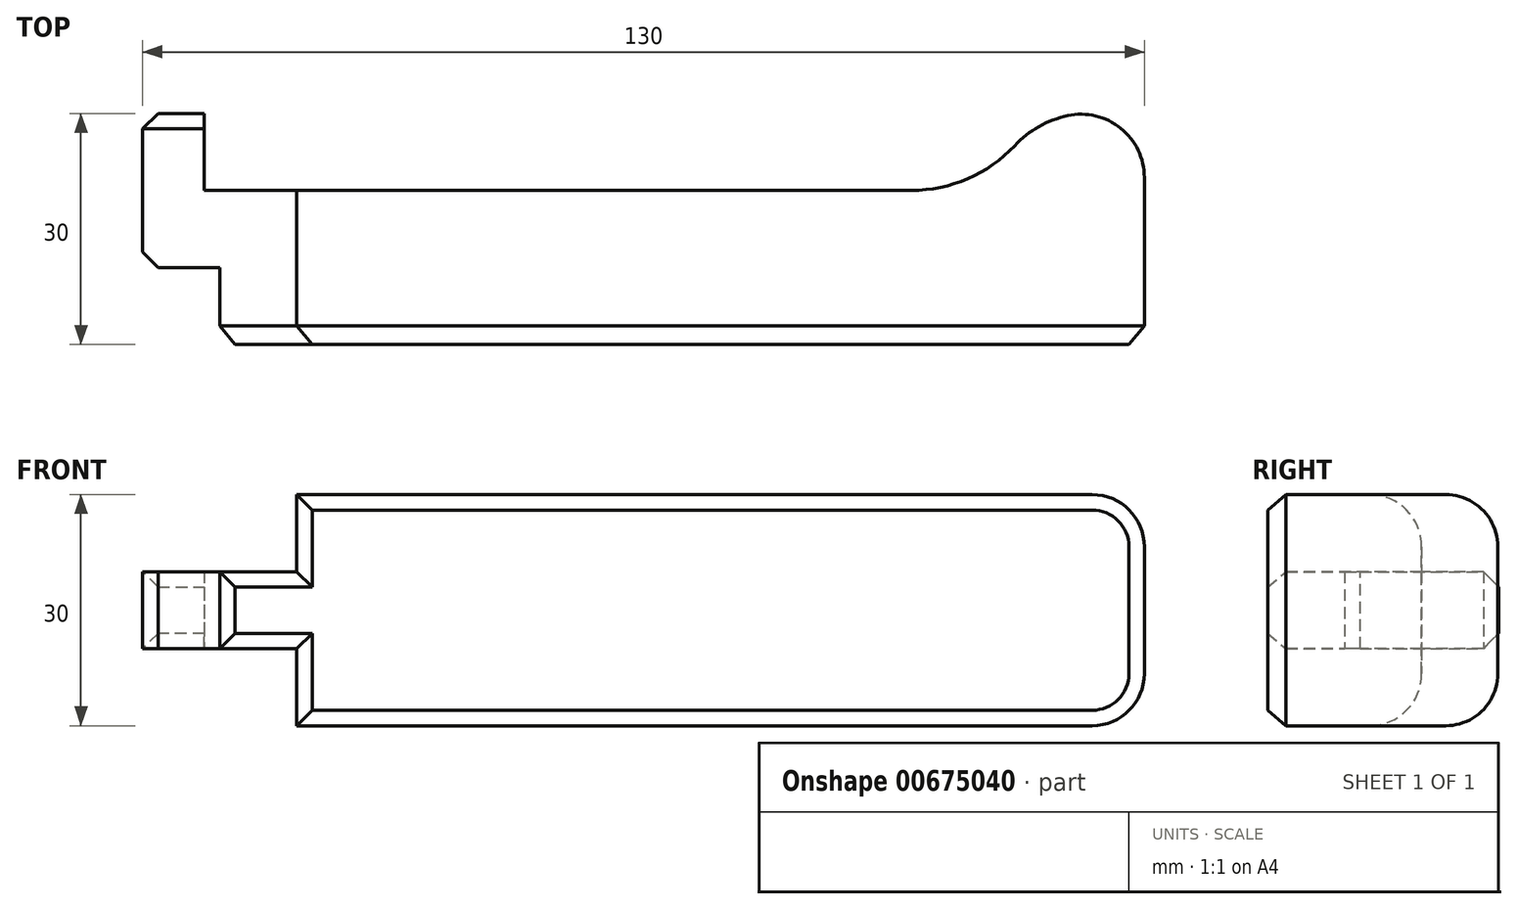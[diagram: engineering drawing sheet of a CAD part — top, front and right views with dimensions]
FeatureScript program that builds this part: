
annotation { "Feature Type Name" : "Feature", "Feature Type Description" : "" }
export const myFeature = defineFeature(function(context is Context, id is Id, definition is map)
    precondition{}
    {
        {
            var Q0;
            Q0=qCreatedBy(makeId("Top.planeOp"),FACE);
            var sketch = newSketch(context, id + "F0", { "sketchPlane" : qUnion([Q0])});
            skLineSegment(sketch, "E0", {"start": v(-58.1, 0) * mm, "end": v(61.9, 0) * mm});
            skLineSegment(sketch, "E1", {"start": v(-58.1, 0) * mm, "end": v(-58.1, 10) * mm});
            skLineSegment(sketch, "E2", {"start": v(-58.1, 10) * mm, "end": v(-68.1, 10) * mm});
            skLineSegment(sketch, "E3", {"start": v(-68.1, 10) * mm, "end": v(-68.1, 30) * mm});
            skLineSegment(sketch, "E4", {"start": v(-68.1, 30) * mm, "end": v(-60.1, 30) * mm});
            skLineSegment(sketch, "E5", {"start": v(-60.1, 30) * mm, "end": v(-60.1, 20) * mm});
            skLineSegment(sketch, "E6", {"start": v(-60.1, 20) * mm, "end": v(-48.1, 20) * mm});
            skLineSegment(sketch, "E7", {"start": v(-48.1, 20) * mm, "end": v(-48.1, 0) * mm});
            skLineSegment(sketch, "E8", {"start": v(61.9, 0) * mm, "end": v(61.9, 20) * mm});
            skLineSegment(sketch, "E9", {"start": v(61.9, 20) * mm, "end": v(-48.1, 20) * mm});
            skLineSegment(sketch, "E10", {"start": v(-48.1, 20) * mm, "end": v(-48.1, 20) * mm});
            skLineSegment(sketch, "E11", {"start": v(61.9, 20) * mm, "end": v(61.9, 30) * mm});
            skLineSegment(sketch, "E12", {"start": v(61.9, 30) * mm, "end": v(41.9, 30) * mm});
            skLineSegment(sketch, "E13", {"start": v(41.9, 20) * mm, "end": v(41.9, 30) * mm});
            skSolve(sketch);
        }
        {
            var Q0;
            {var subQ0=sQuery(id+"F0.wireOp",EDGE,"E1");Q0=makeQuery(id+"F0.imprint","IMPRINT",FACE,{"disambiguationData":[TD([[makeQuery(id+"F0.imprint","IMPRINT",EDGE,{"derivedFrom":subQ0}),-1.0]])]});}
            extrude(context, id + "F1", {"entities" : qUnion([Q0]), "endBound" : BoundingType.SYMMETRIC, "depth" : 10 * mm, "offsetDistance" : 25 * mm});
        }
        {
            var Q0;
            {var subQ2=sQuery(id+"F0.wireOp",EDGE,"E7");Q0=makeQuery(id+"F0.imprint","IMPRINT",FACE,{"disambiguationData":[TD([[makeQuery(id+"F0.imprint","IMPRINT",EDGE,{"derivedFrom":subQ2}),1.0]])]});}
            var Q1;
            {var subQ0=sQuery(id+"F0.wireOp",EDGE,"E11");Q1=makeQuery(id+"F0.imprint","IMPRINT",FACE,{"disambiguationData":[TD([[makeQuery(id+"F0.imprint","IMPRINT",EDGE,{"derivedFrom":subQ0}),1.0]])]});}
            extrude(context, id + "F2", {"entities" : qUnion([Q0, Q1]), "operationType" : NewBodyOperationType.ADD, "endBound" : BoundingType.SYMMETRIC, "depth" : 30 * mm, "offsetDistance" : 25 * mm});
        }
        {
            var Q0;
            Q0=makeQuery(id+"F2.opExtrude","SWEPT_EDGE",EDGE,{"disambiguationData":[OSD([sQuery(id+"F0.wireOp",EDGE,"E12"),sQuery(id+"F0.wireOp",EDGE,"E13")])]});
            fillet(context, id + "F3", {"entities" : qUnion([Q0]), "radius" : 13.28 * mm, "tangentPropagation" : true, "allowEdgeOverflow" : false});
        }
        {
            var Q0;
            Q0=makeQuery(id+"F2.opExtrude","SWEPT_EDGE",EDGE,{"disambiguationData":[OSD([sQuery(id+"F0.wireOp",EDGE,"E11"),sQuery(id+"F0.wireOp",EDGE,"E12")])]});
            fillet(context, id + "F4", {"entities" : qUnion([Q0]), "radius" : 8.2 * mm, "tangentPropagation" : true, "allowEdgeOverflow" : false});
        }
        {
            var Q0;
            Q0=makeQuery(id+"F3.opFillet","BLEND_EDGE",EDGE,{"blendedFrom":[makeQuery(id+"F2.opExtrude","SWEPT_EDGE",EDGE,{"disambiguationData":[OSD([sQuery(id+"F0.wireOp",EDGE,"E12"),sQuery(id+"F0.wireOp",EDGE,"E13")])]}),makeQuery(id+"F2.boolean.opBoolean","MERGE",FACE,{"derivedFrom":[makeQuery(id+"F1.opExtrude","SWEPT_FACE",FACE,{"disambiguationData":[OSD([sQuery(id+"F0.wireOp",EDGE,"E6")])]}),makeQuery(id+"F2.opExtrude","SWEPT_FACE",FACE,{"disambiguationData":[OSD([sQuery(id+"F0.wireOp",EDGE,"E9")])]})]})],"blendedInto":[makeQuery(id+"F2.boolean.opBoolean","MERGE",FACE,{"derivedFrom":[makeQuery(id+"F1.opExtrude","SWEPT_FACE",FACE,{"disambiguationData":[OSD([sQuery(id+"F0.wireOp",EDGE,"E6")])]}),makeQuery(id+"F2.opExtrude","SWEPT_FACE",FACE,{"disambiguationData":[OSD([sQuery(id+"F0.wireOp",EDGE,"E9")])]})]})]});
            fillet(context, id + "F5", {"entities" : qUnion([Q0]), "radius" : 18.4 * mm, "tangentPropagation" : true, "allowEdgeOverflow" : false});
        }
        {
            var Q0;
            Q0=makeQuery(id+"F2.opExtrude","CAP_EDGE",EDGE,{"disambiguationData":[OSD([sQuery(id+"F0.wireOp",EDGE,"E9")])],"isStart":true});
            var Q1;
            Q1=makeQuery(id+"F2.opExtrude","CAP_EDGE",EDGE,{"disambiguationData":[OSD([sQuery(id+"F0.wireOp",EDGE,"E9")])],"isStart":false});
            fillet(context, id + "F6", {"entities" : qUnion([Q0, Q1]), "radius" : 6.76 * mm, "tangentPropagation" : true, "allowEdgeOverflow" : false});
        }
        {
            var Q0;
            Q0=makeQuery(id+"F2.opExtrude","CAP_EDGE",EDGE,{"disambiguationData":[OSD([sQuery(id+"F0.wireOp",EDGE,"E0")])],"isStart":true});
            var Q1;
            Q1=makeQuery(id+"F2.opExtrude","CAP_EDGE",EDGE,{"disambiguationData":[OSD([sQuery(id+"F0.wireOp",EDGE,"E0")])],"isStart":false});
            var Q2;
            {var subQ0=sQuery(id+"F0.wireOp",EDGE,"E0");Q2=makeQuery(id+"F6.opFillet","BLEND_EDGE",EDGE,{"blendedFrom":[makeQuery(id+"F2.opExtrude","CAP_EDGE",EDGE,{"disambiguationData":[OSD([sQuery(id+"F0.wireOp",EDGE,"E8"),sQuery(id+"F0.wireOp",EDGE,"E11")])],"isStart":false}),makeQuery(id+"F2.boolean.opBoolean","MERGE",FACE,{"derivedFrom":[makeQuery(id+"F1.opExtrude","SWEPT_FACE",FACE,{"disambiguationData":[OSD([subQ0])]}),makeQuery(id+"F2.opExtrude","SWEPT_FACE",FACE,{"disambiguationData":[OSD([subQ0])]})]})],"blendedInto":[makeQuery(id+"F2.boolean.opBoolean","MERGE",FACE,{"derivedFrom":[makeQuery(id+"F1.opExtrude","SWEPT_FACE",FACE,{"disambiguationData":[OSD([subQ0])]}),makeQuery(id+"F2.opExtrude","SWEPT_FACE",FACE,{"disambiguationData":[OSD([subQ0])]})]})]});}
            var Q3;
            Q3=makeQuery(id+"F2.opExtrude","SWEPT_EDGE",EDGE,{"disambiguationData":[OSD([sQuery(id+"F0.wireOp",EDGE,"E0"),sQuery(id+"F0.wireOp",EDGE,"E8")])]});
            var Q4;
            {var subQ0=sQuery(id+"F0.wireOp",EDGE,"E0");Q4=makeQuery(id+"F6.opFillet","BLEND_EDGE",EDGE,{"blendedFrom":[makeQuery(id+"F2.opExtrude","CAP_EDGE",EDGE,{"disambiguationData":[OSD([sQuery(id+"F0.wireOp",EDGE,"E8"),sQuery(id+"F0.wireOp",EDGE,"E11")])],"isStart":true}),makeQuery(id+"F2.boolean.opBoolean","MERGE",FACE,{"derivedFrom":[makeQuery(id+"F1.opExtrude","SWEPT_FACE",FACE,{"disambiguationData":[OSD([subQ0])]}),makeQuery(id+"F2.opExtrude","SWEPT_FACE",FACE,{"disambiguationData":[OSD([subQ0])]})]})],"blendedInto":[makeQuery(id+"F2.boolean.opBoolean","MERGE",FACE,{"derivedFrom":[makeQuery(id+"F1.opExtrude","SWEPT_FACE",FACE,{"disambiguationData":[OSD([subQ0])]}),makeQuery(id+"F2.opExtrude","SWEPT_FACE",FACE,{"disambiguationData":[OSD([subQ0])]})]})]});}
            var Q5;
            {var subQ0=sQuery(id+"F0.wireOp",EDGE,"E7");var subQ1=sQuery(id+"F0.wireOp",EDGE,"E0");Q5=makeQuery(id+"F2.boolean.opBoolean","SPLIT",EDGE,{"disambiguationData":[TD([makeQuery(id+"F2.opExtrude","CAP_FACE",FACE,{"disambiguationData":[OSD([subQ1,subQ0,sQuery(id+"F0.wireOp",EDGE,"E8"),sQuery(id+"F0.wireOp",EDGE,"E9"),sQuery(id+"F0.wireOp",EDGE,"E11"),sQuery(id+"F0.wireOp",EDGE,"E12"),sQuery(id+"F0.wireOp",EDGE,"E13")])],"isStart":false})])],"derivedFrom":makeQuery(id+"F2.opExtrude","SWEPT_EDGE",EDGE,{"disambiguationData":[OSD([subQ1,subQ0])]})});}
            var Q6;
            {var subQ0=sQuery(id+"F0.wireOp",EDGE,"E7");var subQ1=sQuery(id+"F0.wireOp",EDGE,"E0");Q6=makeQuery(id+"F2.boolean.opBoolean","SPLIT",EDGE,{"disambiguationData":[TD([makeQuery(id+"F2.opExtrude","CAP_FACE",FACE,{"disambiguationData":[OSD([subQ1,subQ0,sQuery(id+"F0.wireOp",EDGE,"E8"),sQuery(id+"F0.wireOp",EDGE,"E9"),sQuery(id+"F0.wireOp",EDGE,"E11"),sQuery(id+"F0.wireOp",EDGE,"E12"),sQuery(id+"F0.wireOp",EDGE,"E13")])],"isStart":true})])],"derivedFrom":makeQuery(id+"F2.opExtrude","SWEPT_EDGE",EDGE,{"disambiguationData":[OSD([subQ1,subQ0])]})});}
            var Q7;
            Q7=makeQuery(id+"F1.opExtrude","CAP_EDGE",EDGE,{"disambiguationData":[OSD([sQuery(id+"F0.wireOp",EDGE,"E0")])],"isStart":true});
            var Q8;
            Q8=makeQuery(id+"F1.opExtrude","SWEPT_EDGE",EDGE,{"disambiguationData":[OSD([sQuery(id+"F0.wireOp",EDGE,"E0"),sQuery(id+"F0.wireOp",EDGE,"E1")])]});
            var Q9;
            Q9=makeQuery(id+"F1.opExtrude","CAP_EDGE",EDGE,{"disambiguationData":[OSD([sQuery(id+"F0.wireOp",EDGE,"E0")])],"isStart":false});
            chamfer(context, id + "F7", {"entities" : qUnion([Q0, Q1, Q2, Q3, Q4, Q5, Q6, Q7, Q8, Q9]), "chamferType" : ChamferType.OFFSET_ANGLE, "width" : 2 * mm, "oppositeDirection" : false, "angle" : 50 * degree, "tangentPropagation" : true});
        }
        {
            var Q0;
            Q0=makeQuery(id+"F1.opExtrude","SWEPT_EDGE",EDGE,{"disambiguationData":[OSD([sQuery(id+"F0.wireOp",EDGE,"E3"),sQuery(id+"F0.wireOp",EDGE,"E4")])]});
            var Q1;
            Q1=makeQuery(id+"F1.opExtrude","CAP_EDGE",EDGE,{"disambiguationData":[OSD([sQuery(id+"F0.wireOp",EDGE,"E4")])],"isStart":true});
            var Q2;
            Q2=makeQuery(id+"F1.opExtrude","CAP_EDGE",EDGE,{"disambiguationData":[OSD([sQuery(id+"F0.wireOp",EDGE,"E4")])],"isStart":false});
            var Q3;
            Q3=makeQuery(id+"F1.opExtrude","SWEPT_EDGE",EDGE,{"disambiguationData":[OSD([sQuery(id+"F0.wireOp",EDGE,"E2"),sQuery(id+"F0.wireOp",EDGE,"E3")])]});
            chamfer(context, id + "F8", {"entities" : qUnion([Q0, Q1, Q2, Q3]), "width" : 2 * mm, "tangentPropagation" : true});
        }
    });
